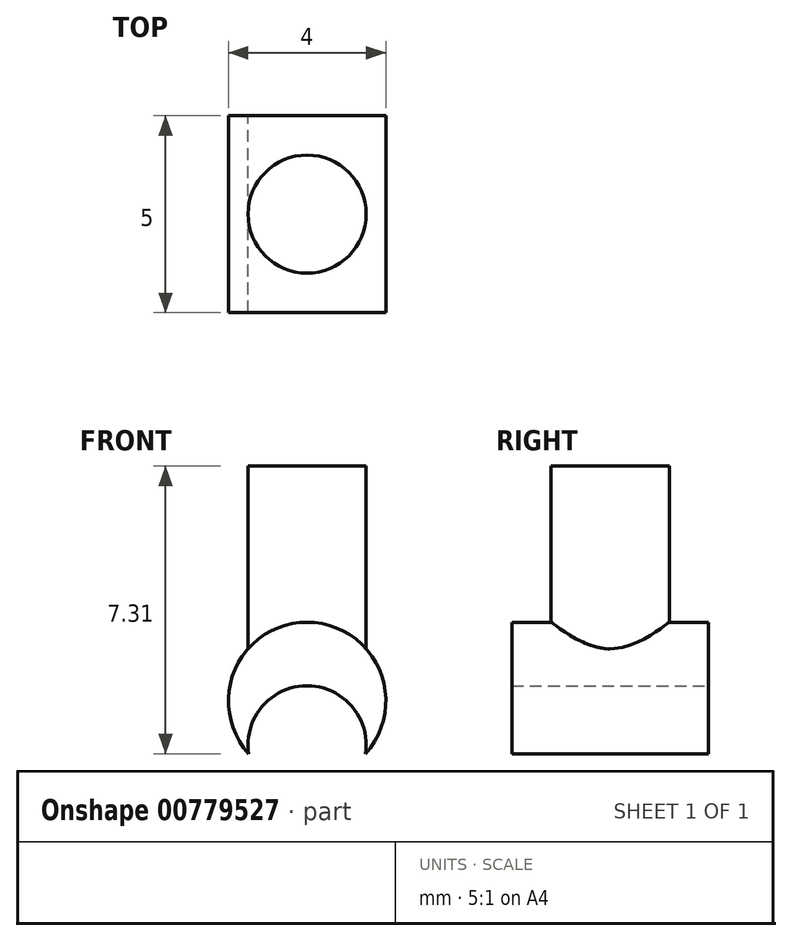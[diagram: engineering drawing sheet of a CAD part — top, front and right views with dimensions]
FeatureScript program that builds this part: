
annotation { "Feature Type Name" : "Feature", "Feature Type Description" : "" }
export const myFeature = defineFeature(function(context is Context, id is Id, definition is map)
    precondition{}
    {
        {
            var Q0;
            Q0=qCreatedBy(makeId("Front.planeOp"),FACE);
            var sketch = newSketch(context, id + "F0", { "sketchPlane" : qUnion([Q0])});
            skPoint(sketch, "E0.center.orphan", {"position": v(0, -2.08) * mm});
            skArc(sketch, "E1", {"start": v(1.48, -2.31) * mm, "mid": v(0, 1.03) * mm, "end": v(-1.48, -2.31) * mm});
            skArc(sketch, "E2", {"start": v(1.48, -2.31) * mm, "mid": v(0, -0.58) * mm, "end": v(-1.48, -2.31) * mm});
            skSolve(sketch);
        }
        {
            var Q0;
            Q0 = qSketchRegion(id + "F0", true);
            extrude(context, id + "F1", {"entities" : qUnion([Q0]), "endBound" : BoundingType.SYMMETRIC, "depth" : 5 * mm, "offsetDistance" : 25 * mm});
        }
        {
            var Q0;
            Q0=qCreatedBy(makeId("Top.planeOp"),FACE);
            var sketch = newSketch(context, id + "F2", { "sketchPlane" : qUnion([Q0])});
            skCircle(sketch, "E3", {"center": v(0, 0) * mm, "radius": 1.5 * mm});
            skSolve(sketch);
        }
        {
            var Q0;
            Q0 = qSketchRegion(id + "F2", true);
            extrude(context, id + "F3", {"entities" : qUnion([Q0]), "operationType" : NewBodyOperationType.ADD, "depth" : 5 * mm, "offsetDistance" : 25 * mm});
        }
    });
